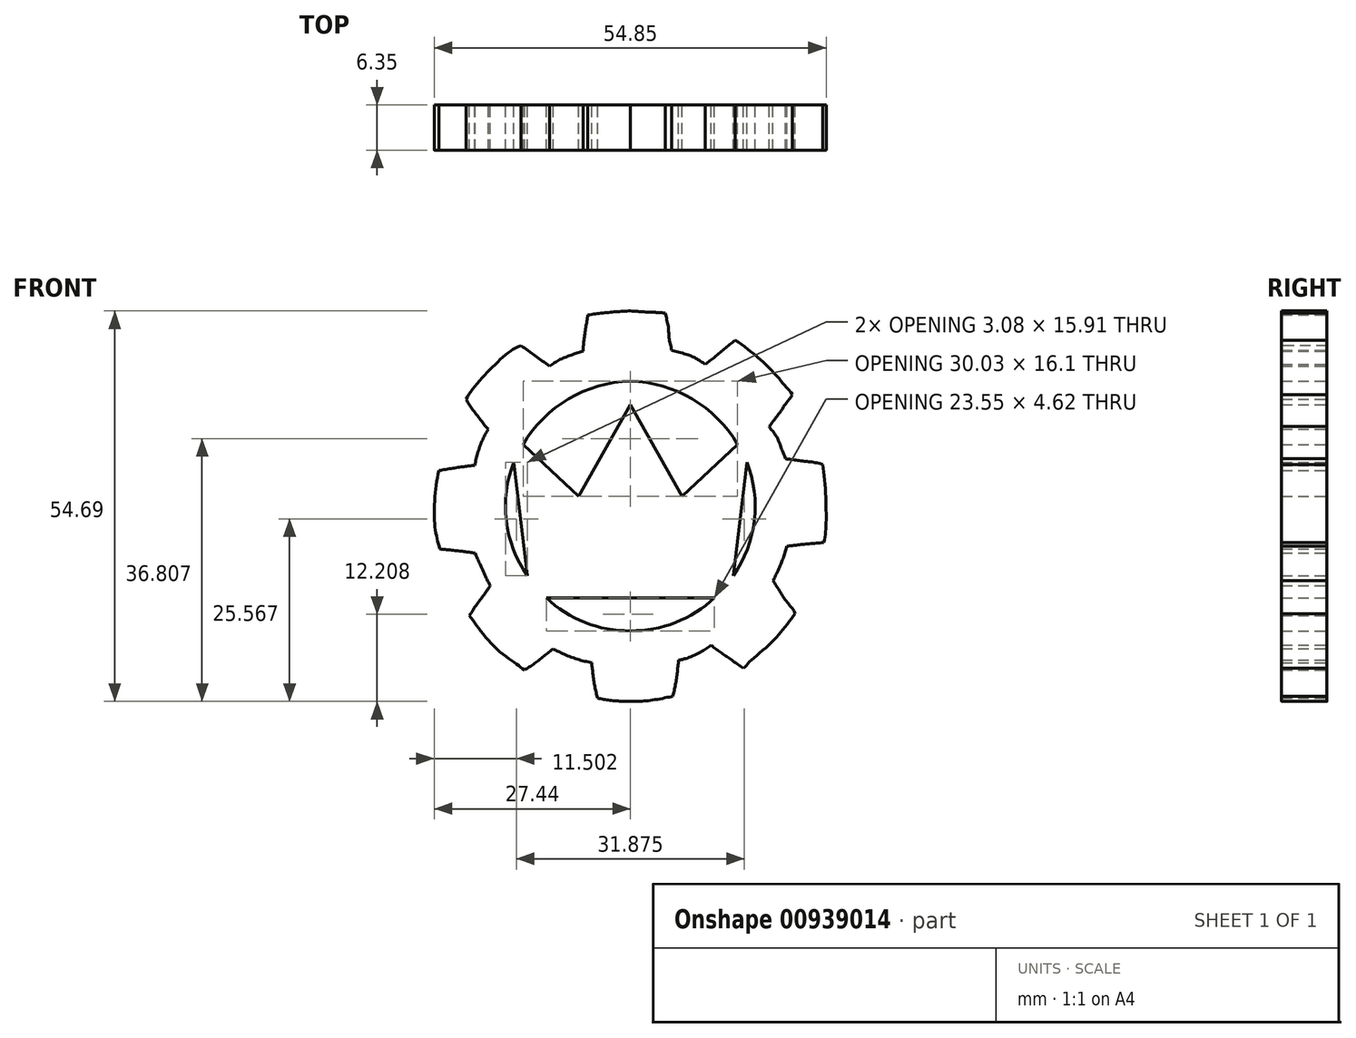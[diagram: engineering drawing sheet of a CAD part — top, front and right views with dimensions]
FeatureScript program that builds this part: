
annotation { "Feature Type Name" : "Feature", "Feature Type Description" : "" }
export const myFeature = defineFeature(function(context is Context, id is Id, definition is map)
    precondition{}
    {
        {
            var Q0;
            Q0=qCreatedBy(makeId("Front.planeOp"),FACE);
            var sketch = newSketch(context, id + "F0", { "sketchPlane" : qUnion([Q0])});
            skFitSpline(sketch, "E0", {"points": [v(0, 29.15) * mm, v(-2.86, 28.96) * mm, v(-5.96, 28.59) * mm], "startDerivative": vector(-5.79, -0.3) * mm, "endDerivative": vector(-6.12, -0.82) * mm});
            skFitSpline(sketch, "E1", {"points": [v(-5.96, 28.59) * mm, v(-6.2, 26.95) * mm, v(-6.48, 25.21) * mm, v(-6.63, 23.5) * mm], "startDerivative": vector(-0.74, -4.95) * mm, "endDerivative": vector(-0.36, -5.13) * mm});
            skFitSpline(sketch, "E2", {"points": [v(-6.63, 23.5) * mm, v(-8.25, 22.99) * mm, v(-9.93, 22.28) * mm, v(-11.28, 21.44) * mm], "startDerivative": vector(-4.8, -1.42) * mm, "endDerivative": vector(-4, -2.73) * mm});
            skFitSpline(sketch, "E3", {"points": [v(-11.28, 21.44) * mm, v(-13.01, 22.65) * mm, v(-15.32, 24.29) * mm], "startDerivative": vector(-3.6, 2.52) * mm, "endDerivative": vector(-4.45, 3.17) * mm});
            skFitSpline(sketch, "E4", {"points": [v(-15.32, 24.29) * mm, v(-16.56, 23.66) * mm, v(-17.86, 22.65) * mm, v(-19.4, 21.18) * mm, v(-20.93, 19.56) * mm, v(-22.27, 17.94) * mm, v(-23, 16.8) * mm], "startDerivative": vector(-8.6, -3.81) * mm, "endDerivative": vector(-4.44, -7.64) * mm});
            skFitSpline(sketch, "E5", {"points": [v(-23, 16.8) * mm, v(-22.32, 15.7) * mm, v(-21.43, 14.5) * mm, v(-20.44, 13.2) * mm, v(-19.88, 12.58) * mm], "startDerivative": vector(2.57, -4.42) * mm, "endDerivative": vector(2.59, -2.75) * mm});
            skFitSpline(sketch, "E6", {"points": [v(-19.88, 12.58) * mm, v(-20.5, 11.47) * mm, v(-21.31, 9.42) * mm, v(-21.77, 7.54) * mm], "startDerivative": vector(-2.16, -3.58) * mm, "endDerivative": vector(-1.08, -5.29) * mm});
            skFitSpline(sketch, "E7", {"points": [v(-21.77, 7.54) * mm, v(-23.77, 7.28) * mm, v(-26.82, 6.8) * mm], "startDerivative": vector(-4.25, -0.5) * mm, "endDerivative": vector(-5.8, -0.97) * mm});
            skFitSpline(sketch, "E8", {"points": [v(-26.82, 6.8) * mm, v(-27.32, 3.45) * mm, v(-27.4, -0.2) * mm, v(-27.11, -2.5) * mm, v(-26.65, -4.18) * mm], "startDerivative": vector(-2.11, -11.65) * mm, "endDerivative": vector(2.48, -8.18) * mm});
            skFitSpline(sketch, "E9", {"points": [v(-26.65, -4.18) * mm, v(-23.79, -4.48) * mm, v(-21.74, -4.74) * mm], "startDerivative": vector(5.55, -0.57) * mm, "endDerivative": vector(4.52, -0.56) * mm});
            skFitSpline(sketch, "E10", {"points": [v(-21.74, -4.74) * mm, v(-20.92, -6.53) * mm, v(-20.08, -8.43) * mm, v(-19.6, -9.3) * mm], "startDerivative": vector(1.76, -4.77) * mm, "endDerivative": vector(1.74, -2.93) * mm});
            skFitSpline(sketch, "E11", {"points": [v(-19.6, -9.3) * mm, v(-20.4, -10.48) * mm, v(-21.74, -12.3) * mm, v(-22.55, -13.5) * mm], "startDerivative": vector(-2.48, -3.52) * mm, "endDerivative": vector(-2.97, -3.23) * mm});
            skFitSpline(sketch, "E12", {"points": [v(-22.55, -13.5) * mm, v(-21.06, -15.5) * mm, v(-18.44, -18.43) * mm, v(-16.06, -20.21) * mm, v(-14.82, -21.13) * mm], "startDerivative": vector(5.6, -7.81) * mm, "endDerivative": vector(5.97, -4.6) * mm});
            skFitSpline(sketch, "E13", {"points": [v(-14.82, -21.13) * mm, v(-13.53, -20.3) * mm, v(-11.93, -19.05) * mm, v(-10.81, -18.16) * mm], "startDerivative": vector(3.86, 2.4) * mm, "endDerivative": vector(3.42, 2.67) * mm});
            skFitSpline(sketch, "E14", {"points": [v(-10.81, -18.16) * mm, v(-9.59, -18.77) * mm, v(-7.45, -19.6) * mm, v(-5.42, -20.11) * mm], "startDerivative": vector(3.96, -2.04) * mm, "endDerivative": vector(5.66, -1.2) * mm});
            skFitSpline(sketch, "E15", {"points": [v(-5.42, -20.11) * mm, v(-5.22, -21.78) * mm, v(-4.94, -23.6) * mm, v(-4.56, -25.07) * mm], "startDerivative": vector(0.58, -4.9) * mm, "endDerivative": vector(1.3, -4.46) * mm});
            skFitSpline(sketch, "E16", {"points": [v(-4.56, -25.07) * mm, v(-2.74, -25.39) * mm, v(-0.82, -25.5) * mm, v(0, -25.54) * mm], "startDerivative": vector(4.52, -1.06) * mm, "endDerivative": vector(2.34, -0.5) * mm});
            skLineSegment(sketch, "E17", {"start": v(0, 16) * mm, "end": v(-7.25, 3.22) * mm});
            skLineSegment(sketch, "E18", {"start": v(-7.25, 3.22) * mm, "end": v(-15.01, 10.46) * mm});
            skArc(sketch, "E19", {"start": v(0, 19.32) * mm, "mid": v(-8.66, 16.84) * mm, "end": v(-15.01, 10.46) * mm});
            skLineSegment(sketch, "E20", {"start": v(-16.3, 7.98) * mm, "end": v(-14.4, -7.93) * mm});
            skArc(sketch, "E21", {"start": v(-16.3, 7.98) * mm, "mid": v(-17.36, -0.21) * mm, "end": v(-14.4, -7.93) * mm});
            skLineSegment(sketch, "E22", {"start": v(-11.78, -11.02) * mm, "end": v(0, -11.02) * mm});
            skArc(sketch, "E23", {"start": v(-11.78, -11.02) * mm, "mid": v(-6.34, -14.48) * mm, "end": v(0, -15.64) * mm});
            skFitSpline(sketch, "E24.MirrorCS", {"points": [v(27.06, -3.28) * mm, v(23.94, -3.56) * mm, v(21.9, -3.8) * mm], "startDerivative": vector(-5.55, -0.57) * mm, "endDerivative": vector(-4.52, -0.56) * mm});
            skFitSpline(sketch, "E25.MirrorCS", {"points": [v(21.9, -3.8) * mm, v(21.41, -5.36) * mm, v(20.77, -6.97) * mm, v(19.97, -8.6) * mm], "startDerivative": vector(-1.76, -4.77) * mm, "endDerivative": vector(-1.74, -2.93) * mm});
            skFitSpline(sketch, "E26.MirrorCS", {"points": [v(15.8, -20.86) * mm, v(13.92, -19.54) * mm, v(12.72, -18.74) * mm, v(11.32, -17.66) * mm], "startDerivative": vector(-3.86, 2.4) * mm, "endDerivative": vector(-3.42, 2.67) * mm});
            skFitSpline(sketch, "E27.MirrorCS", {"points": [v(5.75, 23.67) * mm, v(8.08, 22.99) * mm, v(9.32, 22.43) * mm, v(10.48, 21.67) * mm], "startDerivative": vector(4.8, -1.42) * mm, "endDerivative": vector(4, -2.73) * mm});
            skFitSpline(sketch, "E28.MirrorCS", {"points": [v(19.97, -8.6) * mm, v(20.97, -10.21) * mm, v(22.05, -11.77) * mm, v(23.06, -13.25) * mm], "startDerivative": vector(2.48, -3.52) * mm, "endDerivative": vector(0.37, -3.74) * mm});
            skFitSpline(sketch, "E29.MirrorCS", {"points": [v(19.41, 12.98) * mm, v(20.5, 11.47) * mm, v(21.31, 9.42) * mm, v(21.7, 8.45) * mm], "startDerivative": vector(2.16, -3.58) * mm, "endDerivative": vector(1.08, -5.29) * mm});
            skFitSpline(sketch, "E30.MirrorCS", {"points": [v(10.48, 21.67) * mm, v(12.4, 23.19) * mm, v(14.69, 25.03) * mm], "startDerivative": vector(3.6, 2.52) * mm, "endDerivative": vector(4.45, 3.17) * mm});
            skFitSpline(sketch, "E31.MirrorCS", {"points": [v(5.93, -24.8) * mm, v(2.74, -25.39) * mm, v(0.82, -25.5) * mm, v(0, -25.54) * mm], "startDerivative": vector(-4.52, -1.06) * mm, "endDerivative": vector(-2.34, -0.5) * mm});
            skFitSpline(sketch, "E32.MirrorCS", {"points": [v(22.7, 17.42) * mm, v(21.57, 15.9) * mm, v(21.13, 15.22) * mm, v(20.37, 14.22) * mm, v(19.41, 12.98) * mm], "startDerivative": vector(-2.57, -4.42) * mm, "endDerivative": vector(-2.59, -2.75) * mm});
            skFitSpline(sketch, "E33.MirrorCS", {"points": [v(4.91, 28.84) * mm, v(5.31, 26.87) * mm, v(5.43, 25.27) * mm, v(5.75, 23.67) * mm], "startDerivative": vector(0.74, -4.95) * mm, "endDerivative": vector(0.36, -5.13) * mm});
            skFitSpline(sketch, "E34.MirrorCS", {"points": [v(11.32, -17.66) * mm, v(9.59, -18.77) * mm, v(7.45, -19.6) * mm, v(6.76, -19.74) * mm], "startDerivative": vector(-3.96, -2.04) * mm, "endDerivative": vector(-5.66, -1.2) * mm});
            skFitSpline(sketch, "E35.MirrorCS", {"points": [v(0, 29.15) * mm, v(2.86, 28.96) * mm, v(4.91, 28.84) * mm], "startDerivative": vector(5.79, -0.3) * mm, "endDerivative": vector(6.12, -0.82) * mm});
            skFitSpline(sketch, "E36.MirrorCS", {"points": [v(6.76, -19.74) * mm, v(6.56, -21.62) * mm, v(6.28, -23.35) * mm, v(5.93, -24.8) * mm], "startDerivative": vector(-0.58, -4.9) * mm, "endDerivative": vector(-1.3, -4.46) * mm});
            skFitSpline(sketch, "E37.MirrorCS", {"points": [v(21.7, 8.45) * mm, v(24.14, 8.13) * mm, v(26.9, 7.65) * mm], "startDerivative": vector(4.25, -0.5) * mm, "endDerivative": vector(6.52, -2.1) * mm});
            skFitSpline(sketch, "E38.MirrorCS", {"points": [v(26.9, 7.65) * mm, v(27.32, 3.45) * mm, v(27.4, -0.2) * mm, v(27.34, -1.44) * mm, v(27.06, -3.28) * mm], "startDerivative": vector(2.11, -11.65) * mm, "endDerivative": vector(-2.48, -8.18) * mm});
            skFitSpline(sketch, "E39.MirrorCS", {"points": [v(23.06, -13.25) * mm, v(21.33, -15.5) * mm, v(19.21, -17.78) * mm, v(16.65, -20.02) * mm, v(15.8, -20.86) * mm], "startDerivative": vector(-5.6, -7.81) * mm, "endDerivative": vector(-5.97, -4.6) * mm});
            skFitSpline(sketch, "E40.MirrorCS", {"points": [v(14.69, 25.03) * mm, v(16.56, 23.66) * mm, v(17.86, 22.65) * mm, v(19.4, 21.18) * mm, v(20.93, 19.56) * mm, v(21.7, 18.58) * mm, v(22.7, 17.42) * mm], "startDerivative": vector(8.6, -3.81) * mm, "endDerivative": vector(4.44, -7.64) * mm});
            skArc(sketch, "E41.MirrorCS", {"start": v(16.3, 7.98) * mm, "mid": v(17.36, -0.21) * mm, "end": v(14.4, -7.93) * mm});
            skLineSegment(sketch, "E42.MirrorCS", {"start": v(11.78, -11.02) * mm, "end": v(0, -11.02) * mm});
            skLineSegment(sketch, "E43.MirrorCS", {"start": v(16.3, 7.98) * mm, "end": v(14.4, -7.93) * mm});
            skLineSegment(sketch, "E44.MirrorCS", {"start": v(7.25, 3.22) * mm, "end": v(15.01, 10.46) * mm});
            skArc(sketch, "E45.MirrorCS", {"start": v(0, 19.32) * mm, "mid": v(8.66, 16.84) * mm, "end": v(15.01, 10.46) * mm});
            skLineSegment(sketch, "E46.MirrorCS", {"start": v(0, 16) * mm, "end": v(7.25, 3.22) * mm});
            skArc(sketch, "E47.MirrorCS", {"start": v(11.78, -11.02) * mm, "mid": v(6.34, -14.48) * mm, "end": v(0, -15.64) * mm});
            skSolve(sketch);
        }
        {
            var Q0;
            Q0 = qSketchRegion(id + "F0", true);
            extrude(context, id + "F1", {"entities" : qUnion([Q0]), "depth" : 6.35 * mm, "offsetDistance" : 25.4 * mm});
        }
    });
